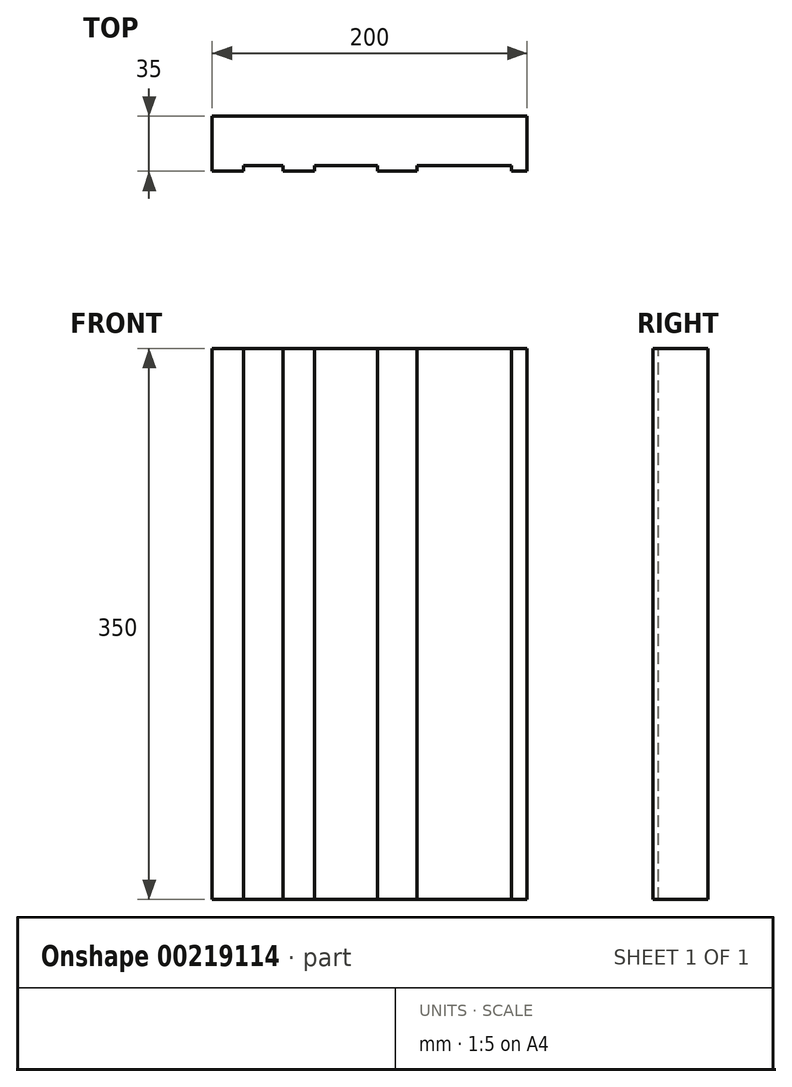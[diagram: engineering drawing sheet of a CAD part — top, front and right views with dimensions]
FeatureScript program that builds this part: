
annotation { "Feature Type Name" : "Feature", "Feature Type Description" : "" }
export const myFeature = defineFeature(function(context is Context, id is Id, definition is map)
    precondition{}
    {
        {
            var Q0;
            Q0=qCreatedBy(makeId("Top.planeOp"),FACE);
            var sketch = newSketch(context, id + "F0", { "sketchPlane" : qUnion([Q0])});
            skLineSegment(sketch, "E0.bottom", {"start": v(-97.73, -45.12) * mm, "end": v(102.27, -45.12) * mm});
            skLineSegment(sketch, "E0.left", {"start": v(-97.73, -45.12) * mm, "end": v(-97.73, -80.12) * mm});
            skLineSegment(sketch, "E0.right", {"start": v(102.27, -45.12) * mm, "end": v(102.27, -80.12) * mm});
            skLineSegment(sketch, "E1.top", {"start": v(-77.73, -76.62) * mm, "end": v(-52.73, -76.62) * mm});
            skLineSegment(sketch, "E1.left", {"start": v(-77.73, -80.12) * mm, "end": v(-77.73, -76.62) * mm});
            skLineSegment(sketch, "E1.right", {"start": v(-52.73, -80.12) * mm, "end": v(-52.73, -76.62) * mm});
            skLineSegment(sketch, "E2.top", {"start": v(-32.73, -76.62) * mm, "end": v(7.27, -76.62) * mm});
            skLineSegment(sketch, "E2.left", {"start": v(-32.73, -80.12) * mm, "end": v(-32.73, -76.62) * mm});
            skLineSegment(sketch, "E2.right", {"start": v(7.27, -80.12) * mm, "end": v(7.27, -76.62) * mm});
            skLineSegment(sketch, "E3.top", {"start": v(32.27, -76.62) * mm, "end": v(92.27, -76.62) * mm});
            skLineSegment(sketch, "E3.left", {"start": v(32.27, -80.12) * mm, "end": v(32.27, -76.62) * mm});
            skLineSegment(sketch, "E3.right", {"start": v(92.27, -80.12) * mm, "end": v(92.27, -76.62) * mm});
            skLineSegment(sketch, "E4.trimOffspring", {"start": v(7.27, -80.12) * mm, "end": v(32.27, -80.12) * mm});
            skLineSegment(sketch, "E5.trimOffspring", {"start": v(92.27, -80.12) * mm, "end": v(102.27, -80.12) * mm});
            skLineSegment(sketch, "E6", {"start": v(-52.73, -80.12) * mm, "end": v(-32.73, -80.12) * mm});
            skLineSegment(sketch, "E7", {"start": v(-77.73, -80.12) * mm, "end": v(-97.73, -80.12) * mm});
            skSolve(sketch);
        }
        {
            var Q0;
            Q0 = qSketchRegion(id + "F0", true);
            extrude(context, id + "F1", {"entities" : qUnion([Q0]), "oppositeDirection" : true, "depth" : 350 * mm});
        }
    });
